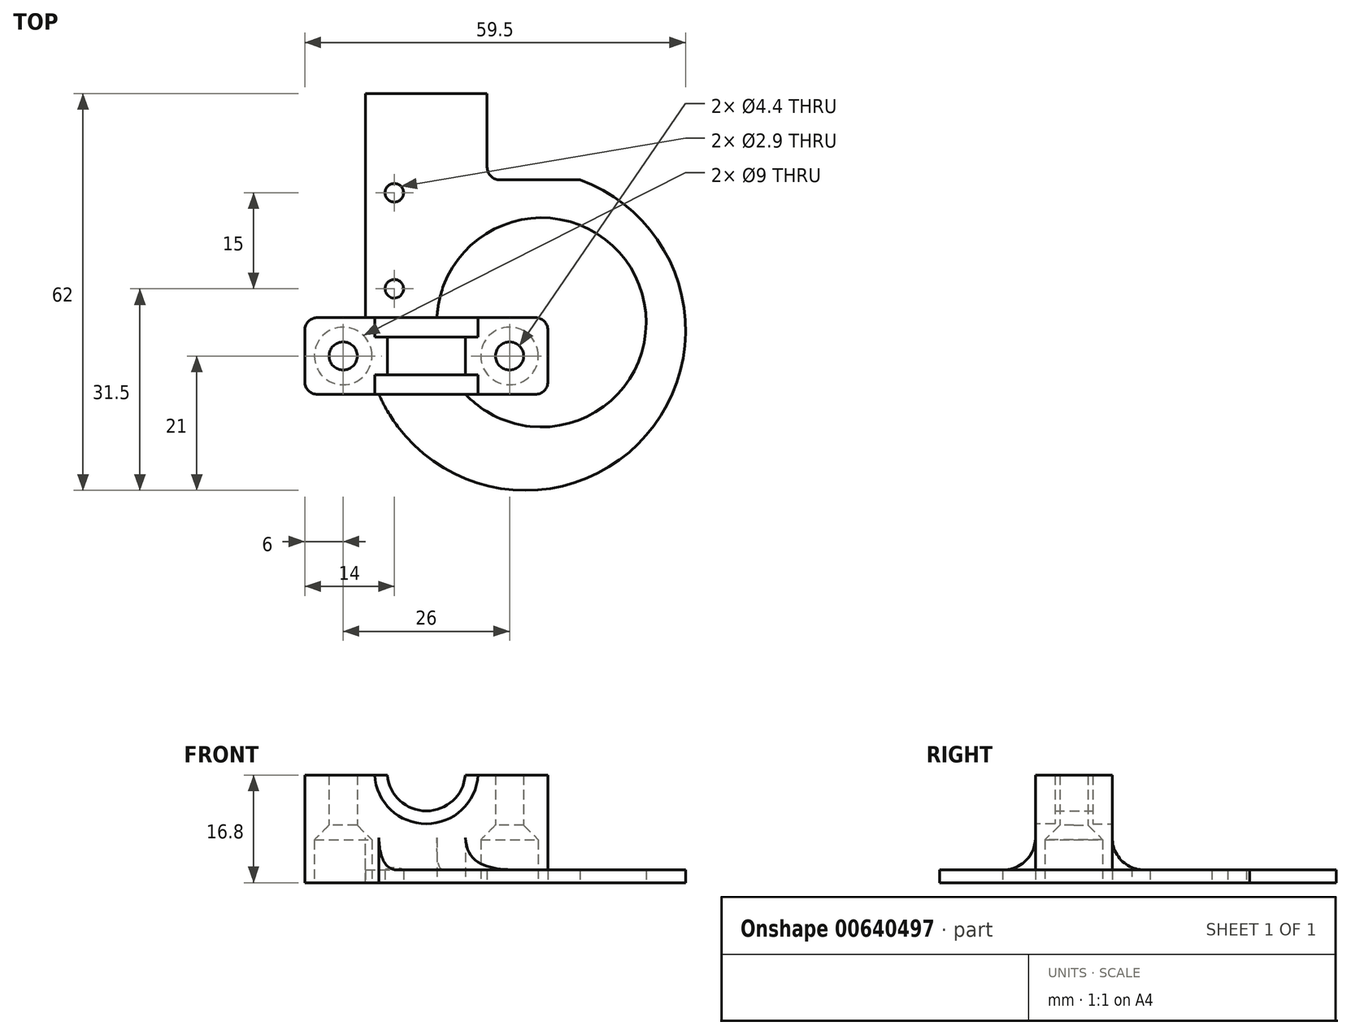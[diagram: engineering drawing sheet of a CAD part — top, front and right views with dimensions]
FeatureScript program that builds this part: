
annotation { "Feature Type Name" : "Feature", "Feature Type Description" : "" }
export const myFeature = defineFeature(function(context is Context, id is Id, definition is map)
    precondition{}
    {
        {
            var Q0;
            Q0=qCreatedBy(makeId("Top.planeOp"),FACE);
            var sketch = newSketch(context, id + "F0", { "sketchPlane" : qUnion([Q0])});
            skLineSegment(sketch, "E0.bottom", {"start": v(-19, 6) * mm, "end": v(19, 6) * mm});
            skLineSegment(sketch, "E0.top", {"start": v(-19, -6) * mm, "end": v(19, -6) * mm});
            skLineSegment(sketch, "E0.left", {"start": v(-19, 6) * mm, "end": v(-19, -6) * mm});
            skLineSegment(sketch, "E0.right", {"start": v(19, 6) * mm, "end": v(19, -6) * mm});
            skCircle(sketch, "E1", {"center": v(-13, 0) * mm, "radius": 2.2 * mm});
            skCircle(sketch, "E2", {"center": v(13, 0) * mm, "radius": 2.2 * mm});
            skSolve(sketch);
        }
        {
            var Q0;
            Q0 = qSketchRegion(id + "F0", true);
            extrude(context, id + "F1", {"entities" : qUnion([Q0]), "depth" : 16.8 * mm, "offsetDistance" : 25 * mm});
        }
        {
            var Q0;
            Q0=makeQuery(id+"F1.opExtrude","SWEPT_FACE",FACE,{"disambiguationData":[OSD([sQuery(id+"F0.wireOp",EDGE,"E0.bottom")])]});
            var sketch = newSketch(context, id + "F2", { "sketchPlane" : qUnion([Q0])});
            skPoint(sketch, "E3.0", {"position": v(0, 16.8) * mm});
            skLineSegment(sketch, "E4.0", {"start": v(19, 16.8) * mm, "end": v(-19, 16.8) * mm});
            skCircle(sketch, "E5", {"center": v(0, 17.3) * mm, "radius": 6.1 * mm});
            skSolve(sketch);
        }
        {
            var Q0;
            Q0 = qSketchRegion(id + "F2", true);
            extrude(context, id + "F3", {"entities" : qUnion([Q0]), "operationType" : NewBodyOperationType.REMOVE, "endBound" : BoundingType.THROUGH_ALL, "oppositeDirection" : true, "depth" : 25 * mm, "offsetDistance" : 25 * mm});
        }
        {
            var Q0;
            Q0=makeQuery(id+"F1.opExtrude","SWEPT_FACE",FACE,{"disambiguationData":[OSD([sQuery(id+"F0.wireOp",EDGE,"E0.bottom")])]});
            var sketch = newSketch(context, id + "F4", { "sketchPlane" : qUnion([Q0])});
            skArc(sketch, "E6.0", {"start": v(-6.08, 16.8) * mm, "mid": v(0, 11.2) * mm, "end": v(6.08, 16.8) * mm});
            skCircle(sketch, "E7", {"center": v(0, 17.3) * mm, "radius": 8.1 * mm});
            skSolve(sketch);
        }
        {
            var Q0;
            Q0 = qSketchRegion(id + "F4", true);
            extrude(context, id + "F5", {"entities" : qUnion([Q0]), "operationType" : NewBodyOperationType.REMOVE, "oppositeDirection" : true, "depth" : 3.05 * mm, "offsetDistance" : 25 * mm});
        }
        {
            var Q0;
            Q0=makeQuery(id+"F1.opExtrude","SWEPT_FACE",FACE,{"disambiguationData":[OSD([sQuery(id+"F0.wireOp",EDGE,"E0.top")])]});
            var sketch = newSketch(context, id + "F6", { "sketchPlane" : qUnion([Q0])});
            skArc(sketch, "E8.0", {"start": v(6.08, 16.8) * mm, "mid": v(0, 11.2) * mm, "end": v(-6.08, 16.8) * mm});
            skCircle(sketch, "E9", {"center": v(0, 17.3) * mm, "radius": 8.1 * mm});
            skSolve(sketch);
        }
        {
            var Q0;
            Q0 = qSketchRegion(id + "F6", true);
            extrude(context, id + "F7", {"entities" : qUnion([Q0]), "operationType" : NewBodyOperationType.REMOVE, "oppositeDirection" : true, "depth" : 3.05 * mm, "offsetDistance" : 25 * mm});
        }
        {
            var Q0;
            Q0=qCreatedBy(makeId("Top.planeOp"),FACE);
            var sketch = newSketch(context, id + "F8", { "sketchPlane" : qUnion([Q0])});
            skLineSegment(sketch, "E10", {"start": v(-9.5, 4) * mm, "end": v(-9.5, 41) * mm});
            skLineSegment(sketch, "E11", {"start": v(-9.5, 41) * mm, "end": v(9.5, 41) * mm});
            skLineSegment(sketch, "E12", {"start": v(9.5, 41) * mm, "end": v(9.5, 27.5) * mm});
            skLineSegment(sketch, "E13", {"start": v(9.5, 27.5) * mm, "end": v(24.03, 27.5) * mm});
            skArc(sketch, "E14", {"start": v(-9.5, 4) * mm, "mid": v(29.85, -16.47) * mm, "end": v(24.03, 27.5) * mm});
            skCircle(sketch, "E15", {"center": v(18, 5.25) * mm, "radius": 16.34 * mm});
            skLineSegment(sketch, "E16", {"start": v(1.65, 41) * mm, "end": v(1.65, -21) * mm, "construction": true});
            skLineSegment(sketch, "E17", {"start": v(34.34, 44.3) * mm, "end": v(34.34, -17.7) * mm, "construction": true});
            skLineSegment(sketch, "E18", {"start": v(-9.5, -11.1) * mm, "end": v(40.5, -11.1) * mm, "construction": true});
            skSolve(sketch);
        }
        {
            var Q0;
            Q0 = qSketchRegion(id + "F8", true);
            extrude(context, id + "F9", {"entities" : qUnion([Q0]), "operationType" : NewBodyOperationType.ADD, "depth" : 2 * mm, "offsetDistance" : 25 * mm});
        }
        {
            var Q0;
            Q0=makeQuery(id+"F9.boolean.opBoolean","MERGE",FACE,{"derivedFrom":[makeQuery(id+"F1.opExtrude","CAP_FACE",FACE,{"disambiguationData":[OSD([sQuery(id+"F0.wireOp",EDGE,"E0.bottom"),sQuery(id+"F0.wireOp",EDGE,"E0.top"),sQuery(id+"F0.wireOp",EDGE,"E0.left"),sQuery(id+"F0.wireOp",EDGE,"E0.right"),sQuery(id+"F0.wireOp",EDGE,"E1"),sQuery(id+"F0.wireOp",EDGE,"E2")])],"isStart":true}),makeQuery(id+"F9.opExtrude","CAP_FACE",FACE,{"disambiguationData":[OSD([sQuery(id+"F8.wireOp",EDGE,"E10"),sQuery(id+"F8.wireOp",EDGE,"E11"),sQuery(id+"F8.wireOp",EDGE,"E12"),sQuery(id+"F8.wireOp",EDGE,"E13"),sQuery(id+"F8.wireOp",EDGE,"E14"),sQuery(id+"F8.wireOp",EDGE,"E15")])],"isStart":true})]});
            var sketch = newSketch(context, id + "F10", { "sketchPlane" : qUnion([Q0])});
            skCircle(sketch, "E19", {"center": v(-5, -10.5) * mm, "radius": 1.45 * mm});
            skCircle(sketch, "E20", {"center": v(-5, -25.5) * mm, "radius": 1.45 * mm});
            skLineSegment(sketch, "E21.0", {"start": v(-9.5, -41) * mm, "end": v(9.5, -41) * mm});
            skLineSegment(sketch, "E22", {"start": v(-5, -25.5) * mm, "end": v(-5, -10.5) * mm, "construction": true});
            skSolve(sketch);
        }
        {
            var Q0;
            Q0 = qSketchRegion(id + "F10", true);
            extrude(context, id + "F11", {"entities" : qUnion([Q0]), "operationType" : NewBodyOperationType.REMOVE, "endBound" : BoundingType.THROUGH_ALL, "oppositeDirection" : true, "depth" : 25 * mm, "offsetDistance" : 25 * mm});
        }
        {
            var Q0;
            Q0=makeQuery(id+"F9.boolean.opBoolean","MERGE",FACE,{"derivedFrom":[makeQuery(id+"F1.opExtrude","CAP_FACE",FACE,{"disambiguationData":[OSD([sQuery(id+"F0.wireOp",EDGE,"E0.bottom"),sQuery(id+"F0.wireOp",EDGE,"E0.top"),sQuery(id+"F0.wireOp",EDGE,"E0.left"),sQuery(id+"F0.wireOp",EDGE,"E0.right"),sQuery(id+"F0.wireOp",EDGE,"E1"),sQuery(id+"F0.wireOp",EDGE,"E2")])],"isStart":true}),makeQuery(id+"F9.opExtrude","CAP_FACE",FACE,{"disambiguationData":[OSD([sQuery(id+"F8.wireOp",EDGE,"E10"),sQuery(id+"F8.wireOp",EDGE,"E11"),sQuery(id+"F8.wireOp",EDGE,"E12"),sQuery(id+"F8.wireOp",EDGE,"E13"),sQuery(id+"F8.wireOp",EDGE,"E14"),sQuery(id+"F8.wireOp",EDGE,"E15")])],"isStart":true})]});
            var sketch = newSketch(context, id + "F12", { "sketchPlane" : qUnion([Q0])});
            skCircle(sketch, "E23.0", {"center": v(-13, 0) * mm, "radius": 2.2 * mm});
            skCircle(sketch, "E24.0", {"center": v(13, 0) * mm, "radius": 2.2 * mm});
            skCircle(sketch, "E25", {"center": v(-13, 0) * mm, "radius": 4.5 * mm});
            skCircle(sketch, "E26", {"center": v(13, 0) * mm, "radius": 4.5 * mm});
            skSolve(sketch);
        }
        {
            var Q0;
            Q0 = qSketchRegion(id + "F12", true);
            extrude(context, id + "F13", {"entities" : qUnion([Q0]), "operationType" : NewBodyOperationType.REMOVE, "oppositeDirection" : true, "depth" : 9 * mm, "offsetDistance" : 25 * mm});
        }
        {
            var Q0;
            Q0=makeQuery(id+"F13.boolean.opBoolean","COPY",EDGE,{"derivedFrom":makeQuery(id+"F13.opExtrude","CAP_EDGE",EDGE,{"disambiguationData":[OSD([sQuery(id+"F12.wireOp",EDGE,"E25")])],"isStart":false})});
            var Q1;
            Q1=makeQuery(id+"F13.boolean.opBoolean","COPY",EDGE,{"derivedFrom":makeQuery(id+"F13.opExtrude","CAP_EDGE",EDGE,{"disambiguationData":[OSD([sQuery(id+"F12.wireOp",EDGE,"E26")])],"isStart":false})});
            chamfer(context, id + "F14", {"entities" : qUnion([Q0, Q1]), "width" : 2.3 * mm, "tangentPropagation" : true});
        }
        {
            var Q0;
            Q0=makeQuery(id+"F9.boolean.opBoolean","INTERSECT",EDGE,{"derivedFrom":[makeQuery(id+"F1.opExtrude","SWEPT_FACE",FACE,{"disambiguationData":[OSD([sQuery(id+"F0.wireOp",EDGE,"E0.bottom")])]}),makeQuery(id+"F9.opExtrude","CAP_FACE",FACE,{"disambiguationData":[OSD([sQuery(id+"F8.wireOp",EDGE,"E10"),sQuery(id+"F8.wireOp",EDGE,"E11"),sQuery(id+"F8.wireOp",EDGE,"E12"),sQuery(id+"F8.wireOp",EDGE,"E13"),sQuery(id+"F8.wireOp",EDGE,"E14"),sQuery(id+"F8.wireOp",EDGE,"E15")])],"isStart":false})]});
            var Q1;
            Q1=makeQuery(id+"F9.boolean.opBoolean","INTERSECT",EDGE,{"derivedFrom":[makeQuery(id+"F1.opExtrude","SWEPT_FACE",FACE,{"disambiguationData":[OSD([sQuery(id+"F0.wireOp",EDGE,"E0.top")])]}),makeQuery(id+"F9.opExtrude","CAP_FACE",FACE,{"disambiguationData":[OSD([sQuery(id+"F8.wireOp",EDGE,"E10"),sQuery(id+"F8.wireOp",EDGE,"E11"),sQuery(id+"F8.wireOp",EDGE,"E12"),sQuery(id+"F8.wireOp",EDGE,"E13"),sQuery(id+"F8.wireOp",EDGE,"E14"),sQuery(id+"F8.wireOp",EDGE,"E15")])],"isStart":false})]});
            fillet(context, id + "F15", {"entities" : qUnion([Q0, Q1]), "radius" : 5 * mm, "tangentPropagation" : true, "allowEdgeOverflow" : false});
        }
        {
            var Q0;
            Q0=makeQuery(id+"F1.opExtrude","SWEPT_EDGE",EDGE,{"disambiguationData":[OSD([sQuery(id+"F0.wireOp",EDGE,"E0.bottom"),sQuery(id+"F0.wireOp",EDGE,"E0.right")])]});
            var Q1;
            Q1=makeQuery(id+"F1.opExtrude","SWEPT_EDGE",EDGE,{"disambiguationData":[OSD([sQuery(id+"F0.wireOp",EDGE,"E0.top"),sQuery(id+"F0.wireOp",EDGE,"E0.right")])]});
            var Q2;
            Q2=makeQuery(id+"F1.opExtrude","SWEPT_EDGE",EDGE,{"disambiguationData":[OSD([sQuery(id+"F0.wireOp",EDGE,"E0.bottom"),sQuery(id+"F0.wireOp",EDGE,"E0.left")])]});
            var Q3;
            Q3=makeQuery(id+"F1.opExtrude","SWEPT_EDGE",EDGE,{"disambiguationData":[OSD([sQuery(id+"F0.wireOp",EDGE,"E0.top"),sQuery(id+"F0.wireOp",EDGE,"E0.left")])]});
            var Q4;
            Q4=makeQuery(id+"F9.opExtrude","SWEPT_EDGE",EDGE,{"disambiguationData":[OSD([sQuery(id+"F8.wireOp",EDGE,"E12"),sQuery(id+"F8.wireOp",EDGE,"E13")])]});
            fillet(context, id + "F16", {"entities" : qUnion([Q0, Q1, Q2, Q3, Q4]), "radius" : 2 * mm, "tangentPropagation" : true, "allowEdgeOverflow" : false});
        }
    });
